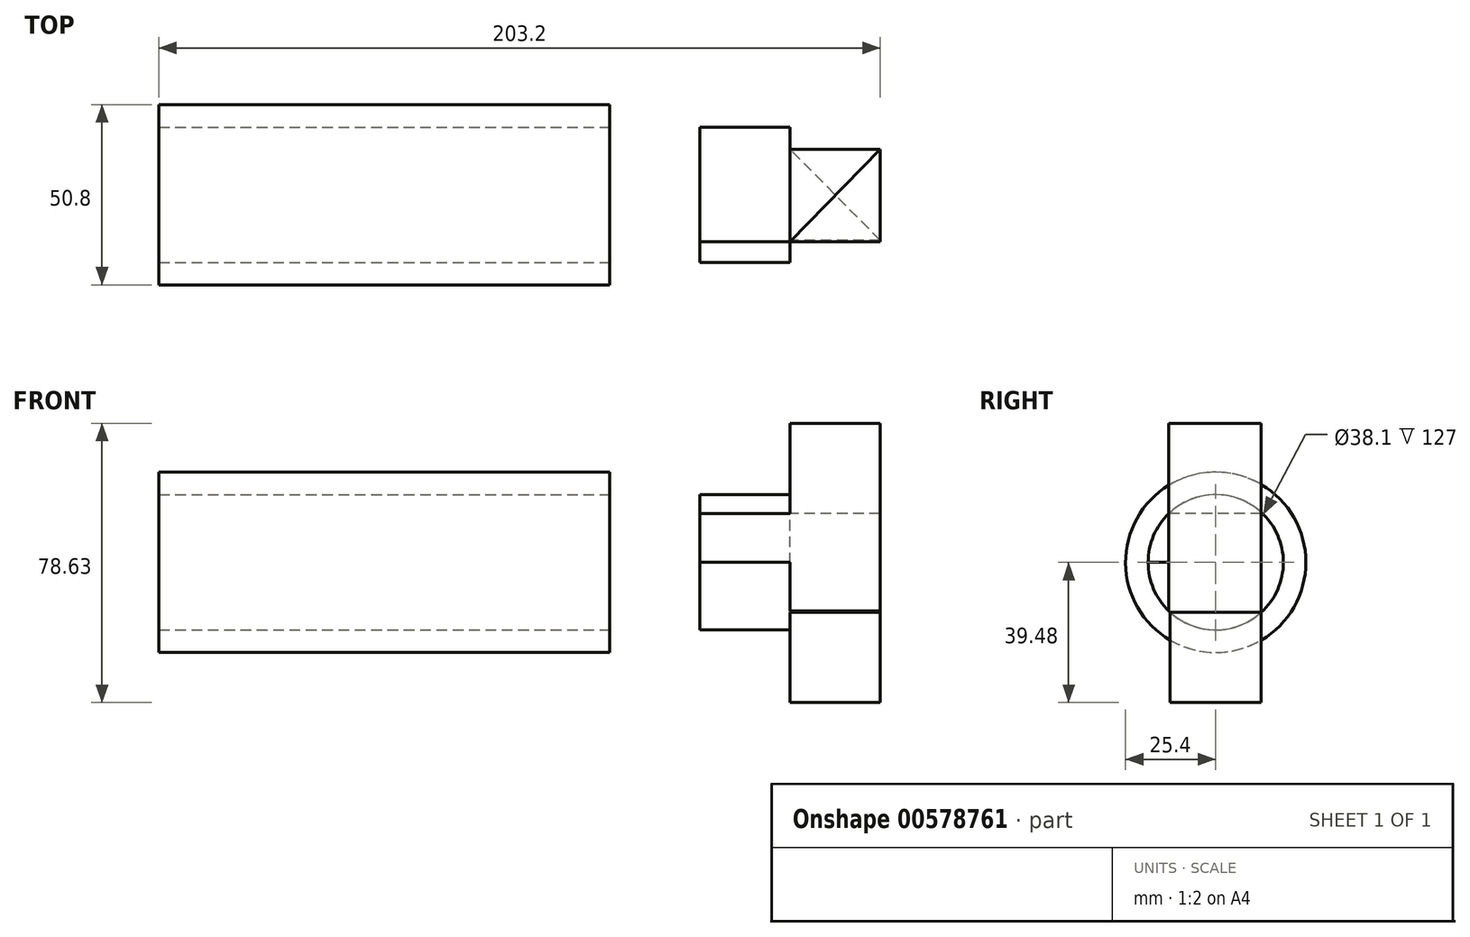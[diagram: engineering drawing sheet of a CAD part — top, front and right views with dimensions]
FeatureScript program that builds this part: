
annotation { "Feature Type Name" : "Feature", "Feature Type Description" : "" }
export const myFeature = defineFeature(function(context is Context, id is Id, definition is map)
    precondition{}
    {
        {
            var Q0;
            Q0=qCreatedBy(makeId("Right.planeOp"),FACE);
            var sketch = newSketch(context, id + "F0", { "sketchPlane" : qUnion([Q0])});
            skCircle(sketch, "E0", {"center": v(0, 0) * mm, "radius": 19.05 * mm});
            skLineSegment(sketch, "E1", {"start": v(19.05, 0) * mm, "end": v(0, 0) * mm});
            skLineSegment(sketch, "E2", {"start": v(0, 0) * mm, "end": v(-19.05, 0) * mm});
            skLineSegment(sketch, "E3", {"start": v(-19.05, 0) * mm, "end": v(0, 0) * mm});
            skLineSegment(sketch, "E4", {"start": v(0, 19.05) * mm, "end": v(0, 0) * mm});
            skLineSegment(sketch, "E5", {"start": v(0, 0) * mm, "end": v(0, -19.05) * mm});
            skLineSegment(sketch, "E6.bottom", {"start": v(12.83, -14.08) * mm, "end": v(-13.18, -14.08) * mm});
            skLineSegment(sketch, "E6.top", {"start": v(12.83, 13.75) * mm, "end": v(-13.18, 13.75) * mm});
            skLineSegment(sketch, "E6.left", {"start": v(12.83, -14.08) * mm, "end": v(12.83, 13.75) * mm});
            skLineSegment(sketch, "E6.right", {"start": v(-13.18, -14.08) * mm, "end": v(-13.18, 13.75) * mm});
            skSolve(sketch);
        }
        {
            var Q0;
            {var subQ0=sQuery(id+"F0.wireOp",EDGE,"E5");var subQ5=sQuery(id+"F0.wireOp",EDGE,"E6.bottom");var subQ6=makeQuery(id+"F0.imprint","INTERSECT",VERTEX,{"derivedFrom":[subQ0,subQ5]});Q0=makeQuery(id+"F0.imprint","IMPRINT",FACE,{"disambiguationData":[TD([[makeQuery(id+"F0.imprint","IMPRINT",EDGE,{"disambiguationData":[TD([[subQ6,1.0]])],"derivedFrom":subQ5}),-1.0]])]});}
            var Q1;
            {var subQ1=sQuery(id+"F0.wireOp",EDGE,"E0");var subQ7=sQuery(id+"F0.wireOp",EDGE,"E6.right");var subQ9=makeQuery(id+"F0.imprint","INTERSECT",VERTEX,{"derivedFrom":[subQ1,subQ7]});Q1=makeQuery(id+"F0.imprint","IMPRINT",FACE,{"disambiguationData":[TD([[makeQuery(id+"F0.imprint","IMPRINT",EDGE,{"disambiguationData":[TD([[subQ9,-1.0]])],"derivedFrom":subQ1}),1.0]])]});}
            var Q2;
            {var subQ0=sQuery(id+"F0.wireOp",EDGE,"E4");var subQ5=sQuery(id+"F0.wireOp",EDGE,"E6.top");var subQ6=makeQuery(id+"F0.imprint","INTERSECT",VERTEX,{"derivedFrom":[subQ0,subQ5]});Q2=makeQuery(id+"F0.imprint","IMPRINT",FACE,{"disambiguationData":[TD([[makeQuery(id+"F0.imprint","IMPRINT",EDGE,{"disambiguationData":[TD([[subQ6,-1.0]])],"derivedFrom":subQ5}),1.0]])]});}
            var Q3;
            {var subQ3=sQuery(id+"F0.wireOp",EDGE,"E6.left");var subQ5=sQuery(id+"F0.wireOp",EDGE,"E6.top");var subQ6=makeQuery(id+"F0.imprint","INTERSECT",VERTEX,{"derivedFrom":[subQ5,subQ3]});Q3=makeQuery(id+"F0.imprint","IMPRINT",FACE,{"disambiguationData":[TD([[makeQuery(id+"F0.imprint","IMPRINT",EDGE,{"disambiguationData":[TD([[subQ6,-1.0]])],"derivedFrom":subQ5}),1.0]])]});}
            extrude(context, id + "F1", {"entities" : qUnion([Q0, Q1, Q2, Q3]), "depth" : 25.4 * mm, "offsetDistance" : 25.4 * mm});
        }
        {
            var Q0;
            {var subQ0=sQuery(id+"F0.wireOp",EDGE,"E5");var subQ1=sQuery(id+"F0.wireOp",EDGE,"E0");var subQ2=makeQuery(id+"F0.imprint","INTERSECT",VERTEX,{"derivedFrom":[subQ1,subQ0]});Q0=makeQuery(id+"F0.imprint","IMPRINT",FACE,{"disambiguationData":[TD([[makeQuery(id+"F0.imprint","IMPRINT",EDGE,{"disambiguationData":[TD([[subQ2,1.0]])],"derivedFrom":subQ1}),1.0]])]});}
            var Q1;
            {var subQ0=sQuery(id+"F0.wireOp",EDGE,"E5");var subQ1=sQuery(id+"F0.wireOp",EDGE,"E0");var subQ2=makeQuery(id+"F0.imprint","INTERSECT",VERTEX,{"derivedFrom":[subQ1,subQ0]});Q1=makeQuery(id+"F0.imprint","IMPRINT",FACE,{"disambiguationData":[TD([[makeQuery(id+"F0.imprint","IMPRINT",EDGE,{"disambiguationData":[TD([[subQ2,1.0]])],"derivedFrom":subQ0}),1.0]])]});}
            var Q2;
            {var subQ0=sQuery(id+"F0.wireOp",EDGE,"E1");var subQ1=sQuery(id+"F0.wireOp",EDGE,"E0");var subQ2=makeQuery(id+"F0.imprint","INTERSECT",VERTEX,{"derivedFrom":[subQ1,subQ0]});Q2=makeQuery(id+"F0.imprint","IMPRINT",FACE,{"disambiguationData":[TD([[makeQuery(id+"F0.imprint","IMPRINT",EDGE,{"disambiguationData":[TD([[subQ2,-1.0]])],"derivedFrom":subQ0}),1.0]])]});}
            var Q3;
            {var subQ0=sQuery(id+"F0.wireOp",EDGE,"E5");var subQ5=sQuery(id+"F0.wireOp",EDGE,"E6.bottom");var subQ6=makeQuery(id+"F0.imprint","INTERSECT",VERTEX,{"derivedFrom":[subQ0,subQ5]});Q3=makeQuery(id+"F0.imprint","IMPRINT",FACE,{"disambiguationData":[TD([[makeQuery(id+"F0.imprint","IMPRINT",EDGE,{"disambiguationData":[TD([[subQ6,1.0]])],"derivedFrom":subQ5}),-1.0]])]});}
            var Q4;
            {var subQ1=sQuery(id+"F0.wireOp",EDGE,"E0");var subQ7=sQuery(id+"F0.wireOp",EDGE,"E6.right");var subQ9=makeQuery(id+"F0.imprint","INTERSECT",VERTEX,{"derivedFrom":[subQ1,subQ7]});Q4=makeQuery(id+"F0.imprint","IMPRINT",FACE,{"disambiguationData":[TD([[makeQuery(id+"F0.imprint","IMPRINT",EDGE,{"disambiguationData":[TD([[subQ9,-1.0]])],"derivedFrom":subQ1}),1.0]])]});}
            var Q5;
            {var subQ0=sQuery(id+"F0.wireOp",EDGE,"E3");var subQ1=sQuery(id+"F0.wireOp",EDGE,"E0");var subQ2=makeQuery(id+"F0.imprint","INTERSECT",VERTEX,{"derivedFrom":[subQ1,subQ0]});Q5=makeQuery(id+"F0.imprint","IMPRINT",FACE,{"disambiguationData":[TD([[makeQuery(id+"F0.imprint","IMPRINT",EDGE,{"disambiguationData":[TD([[subQ2,-1.0]])],"derivedFrom":subQ1}),1.0]])]});}
            var Q6;
            {var subQ0=sQuery(id+"F0.wireOp",EDGE,"E3");var subQ1=sQuery(id+"F0.wireOp",EDGE,"E0");var subQ2=makeQuery(id+"F0.imprint","INTERSECT",VERTEX,{"derivedFrom":[subQ1,subQ0]});Q6=makeQuery(id+"F0.imprint","IMPRINT",FACE,{"disambiguationData":[TD([[makeQuery(id+"F0.imprint","IMPRINT",EDGE,{"disambiguationData":[TD([[subQ2,-1.0]])],"derivedFrom":subQ0}),1.0]])]});}
            var Q7;
            {var subQ0=sQuery(id+"F0.wireOp",EDGE,"E4");var subQ5=sQuery(id+"F0.wireOp",EDGE,"E6.top");var subQ6=makeQuery(id+"F0.imprint","INTERSECT",VERTEX,{"derivedFrom":[subQ0,subQ5]});Q7=makeQuery(id+"F0.imprint","IMPRINT",FACE,{"disambiguationData":[TD([[makeQuery(id+"F0.imprint","IMPRINT",EDGE,{"disambiguationData":[TD([[subQ6,-1.0]])],"derivedFrom":subQ5}),1.0]])]});}
            var Q8;
            {var subQ0=sQuery(id+"F0.wireOp",EDGE,"E4");var subQ1=sQuery(id+"F0.wireOp",EDGE,"E0");var subQ2=makeQuery(id+"F0.imprint","INTERSECT",VERTEX,{"derivedFrom":[subQ1,subQ0]});Q8=makeQuery(id+"F0.imprint","IMPRINT",FACE,{"disambiguationData":[TD([[makeQuery(id+"F0.imprint","IMPRINT",EDGE,{"disambiguationData":[TD([[subQ2,-1.0]])],"derivedFrom":subQ0}),-1.0]])]});}
            var Q9;
            {var subQ5=sQuery(id+"F0.wireOp",EDGE,"E1");var subQ6=sQuery(id+"F0.wireOp",EDGE,"E0");var subQ7=makeQuery(id+"F0.imprint","INTERSECT",VERTEX,{"derivedFrom":[subQ6,subQ5]});Q9=makeQuery(id+"F0.imprint","IMPRINT",FACE,{"disambiguationData":[TD([[makeQuery(id+"F0.imprint","IMPRINT",EDGE,{"disambiguationData":[TD([[subQ7,-1.0]])],"derivedFrom":subQ6}),1.0]])]});}
            var Q10;
            {var subQ3=sQuery(id+"F0.wireOp",EDGE,"E6.left");var subQ5=sQuery(id+"F0.wireOp",EDGE,"E6.top");var subQ6=makeQuery(id+"F0.imprint","INTERSECT",VERTEX,{"derivedFrom":[subQ5,subQ3]});Q10=makeQuery(id+"F0.imprint","IMPRINT",FACE,{"disambiguationData":[TD([[makeQuery(id+"F0.imprint","IMPRINT",EDGE,{"disambiguationData":[TD([[subQ6,-1.0]])],"derivedFrom":subQ5}),1.0]])]});}
            extrude(context, id + "F2", {"entities" : qUnion([Q0, Q1, Q2, Q3, Q4, Q5, Q6, Q7, Q8, Q9, Q10]), "operationType" : NewBodyOperationType.ADD, "oppositeDirection" : true, "depth" : 25.4 * mm, "offsetDistance" : 25.4 * mm});
        }
        {
            var Q0;
            Q0=makeQuery(id+"F1.opExtrude","SWEPT_FACE",FACE,{"disambiguationData":[OSD([sQuery(id+"F0.wireOp",EDGE,"E6.top")])]});
            var sketch = newSketch(context, id + "F3", { "sketchPlane" : qUnion([Q0])});
            skLineSegment(sketch, "E7", {"start": v(0, 12.83) * mm, "end": v(25.4, -13.18) * mm});
            skLineSegment(sketch, "E8", {"start": v(25.4, -13.18) * mm, "end": v(25.4, 12.83) * mm});
            skLineSegment(sketch, "E9", {"start": v(25.4, 12.83) * mm, "end": v(0, -13.18) * mm});
            skCircle(sketch, "E10", {"center": v(12.7, -0.18) * mm, "radius": 3.81 * mm});
            skSolve(sketch);
        }
        {
            var Q0;
            Q0=makeQuery(id+"F1.opExtrude","SWEPT_FACE",FACE,{"disambiguationData":[OSD([sQuery(id+"F0.wireOp",EDGE,"E6.bottom")])]});
            var sketch = newSketch(context, id + "F4", { "sketchPlane" : qUnion([Q0])});
            skLineSegment(sketch, "E11", {"start": v(25.4, -12.83) * mm, "end": v(0, 12.83) * mm});
            skLineSegment(sketch, "E12", {"start": v(0, 12.83) * mm, "end": v(25.4, 12.83) * mm});
            skLineSegment(sketch, "E13", {"start": v(25.4, 12.83) * mm, "end": v(0, -12.83) * mm});
            skCircle(sketch, "E14", {"center": v(12.7, 0) * mm, "radius": 3.81 * mm});
            skSolve(sketch);
        }
        {
            var Q0;
            {var subQ0=sQuery(id+"F3.wireOp",EDGE,"E10");var subQ1=sQuery(id+"F3.wireOp",EDGE,"E7");var subQ2=makeQuery(id+"F3.imprint","INTERSECT",VERTEX,{"disambiguationData":[OD(0.0)],"derivedFrom":[subQ1,subQ0]});Q0=makeQuery(id+"F3.imprint","IMPRINT",FACE,{"disambiguationData":[TD([[makeQuery(id+"F3.imprint","IMPRINT",EDGE,{"disambiguationData":[TD([[subQ2,-1.0]])],"derivedFrom":subQ1}),1.0]])]});}
            var Q1;
            {var subQ0=sQuery(id+"F3.wireOp",EDGE,"E10");var subQ1=sQuery(id+"F3.wireOp",EDGE,"E7");var subQ2=makeQuery(id+"F3.imprint","INTERSECT",VERTEX,{"disambiguationData":[OD(0.0)],"derivedFrom":[subQ1,subQ0]});Q1=makeQuery(id+"F3.imprint","IMPRINT",FACE,{"disambiguationData":[TD([[makeQuery(id+"F3.imprint","IMPRINT",EDGE,{"disambiguationData":[TD([[subQ2,-1.0]])],"derivedFrom":subQ1}),-1.0]])]});}
            var Q2;
            {var subQ0=sQuery(id+"F3.wireOp",EDGE,"E9");var subQ1=sQuery(id+"F3.wireOp",EDGE,"E7");var subQ2=makeQuery(id+"F3.imprint","INTERSECT",VERTEX,{"derivedFrom":[subQ1,subQ0]});Q2=makeQuery(id+"F3.imprint","IMPRINT",FACE,{"disambiguationData":[TD([[makeQuery(id+"F3.imprint","IMPRINT",EDGE,{"disambiguationData":[TD([[subQ2,-1.0]])],"derivedFrom":subQ1}),-1.0]])]});}
            var Q3;
            {var subQ0=sQuery(id+"F3.wireOp",EDGE,"E9");var subQ1=sQuery(id+"F3.wireOp",EDGE,"E7");var subQ2=makeQuery(id+"F3.imprint","INTERSECT",VERTEX,{"derivedFrom":[subQ1,subQ0]});Q3=makeQuery(id+"F3.imprint","IMPRINT",FACE,{"disambiguationData":[TD([[makeQuery(id+"F3.imprint","IMPRINT",EDGE,{"disambiguationData":[TD([[subQ2,-1.0]])],"derivedFrom":subQ1}),1.0]])]});}
            extrude(context, id + "F5", {"entities" : qUnion([Q0, Q1, Q2, Q3]), "operationType" : NewBodyOperationType.ADD, "depth" : 25.4 * mm, "offsetDistance" : 25.4 * mm});
        }
        {
            var Q0;
            {var subQ0=sQuery(id+"F4.wireOp",EDGE,"E14");var subQ1=sQuery(id+"F4.wireOp",EDGE,"E11");var subQ2=makeQuery(id+"F4.imprint","INTERSECT",VERTEX,{"disambiguationData":[OD(0.0)],"derivedFrom":[subQ1,subQ0]});Q0=makeQuery(id+"F4.imprint","IMPRINT",FACE,{"disambiguationData":[TD([[makeQuery(id+"F4.imprint","IMPRINT",EDGE,{"disambiguationData":[TD([[subQ2,-1.0]])],"derivedFrom":subQ1}),1.0]])]});}
            var Q1;
            {var subQ0=sQuery(id+"F4.wireOp",EDGE,"E14");var subQ1=sQuery(id+"F4.wireOp",EDGE,"E11");var subQ2=makeQuery(id+"F4.imprint","INTERSECT",VERTEX,{"disambiguationData":[OD(0.0)],"derivedFrom":[subQ1,subQ0]});Q1=makeQuery(id+"F4.imprint","IMPRINT",FACE,{"disambiguationData":[TD([[makeQuery(id+"F4.imprint","IMPRINT",EDGE,{"disambiguationData":[TD([[subQ2,-1.0]])],"derivedFrom":subQ1}),-1.0]])]});}
            var Q2;
            {var subQ0=sQuery(id+"F4.wireOp",EDGE,"E13");var subQ1=sQuery(id+"F4.wireOp",EDGE,"E11");var subQ2=makeQuery(id+"F4.imprint","INTERSECT",VERTEX,{"derivedFrom":[subQ1,subQ0]});Q2=makeQuery(id+"F4.imprint","IMPRINT",FACE,{"disambiguationData":[TD([[makeQuery(id+"F4.imprint","IMPRINT",EDGE,{"disambiguationData":[TD([[subQ2,-1.0]])],"derivedFrom":subQ1}),-1.0]])]});}
            var Q3;
            {var subQ0=sQuery(id+"F4.wireOp",EDGE,"E13");var subQ1=sQuery(id+"F4.wireOp",EDGE,"E11");var subQ2=makeQuery(id+"F4.imprint","INTERSECT",VERTEX,{"derivedFrom":[subQ1,subQ0]});Q3=makeQuery(id+"F4.imprint","IMPRINT",FACE,{"disambiguationData":[TD([[makeQuery(id+"F4.imprint","IMPRINT",EDGE,{"disambiguationData":[TD([[subQ2,-1.0]])],"derivedFrom":subQ1}),1.0]])]});}
            extrude(context, id + "F6", {"entities" : qUnion([Q0, Q1, Q2, Q3]), "operationType" : NewBodyOperationType.ADD, "depth" : 25.4 * mm, "offsetDistance" : 25.4 * mm});
        }
        {
            var Q0;
            Q0=makeQuery(id+"F2.opExtrude","CAP_FACE",FACE,{"disambiguationData":[OSD([sQuery(id+"F0.wireOp",EDGE,"E0")])],"isStart":false});
            cPlane(context, id + "F7", {"entities" : qUnion([Q0]), "cplaneType" : CPlaneType.OFFSET, "offset" : 25.4 * mm, "width" : 152.4 * mm, "height" : 152.4 * mm});
        }
        {
            var Q0;
            Q0=qCreatedBy(id+"F7.planeOp",FACE);
            var sketch = newSketch(context, id + "F8", { "sketchPlane" : qUnion([Q0])});
            skCircle(sketch, "E15", {"center": v(0, 0) * mm, "radius": 25.4 * mm});
            skSolve(sketch);
        }
        {
            var Q0;
            Q0=makeQuery(id+"F8.imprint","IMPRINT",FACE,{"disambiguationData":[TD([[makeQuery(id+"F8.imprint","IMPRINT",EDGE,{"derivedFrom":sQuery(id+"F8.wireOp",EDGE,"E15")}),1.0]])]});
            extrude(context, id + "F9", {"entities" : qUnion([Q0]), "depth" : 127 * mm, "offsetDistance" : 25.4 * mm});
        }
        {
            var Q0;
            Q0=makeQuery(id+"F9.opExtrude","CAP_FACE",FACE,{"disambiguationData":[OSD([sQuery(id+"F8.wireOp",EDGE,"E15")])],"isStart":true});
            var sketch = newSketch(context, id + "F10", { "sketchPlane" : qUnion([Q0])});
            skLineSegment(sketch, "E16", {"start": v(25.4, 0) * mm, "end": v(-25.4, 0) * mm});
            skLineSegment(sketch, "E17", {"start": v(0, 25.4) * mm, "end": v(0, -25.4) * mm});
            skPoint(sketch, "E18", {"position": v(0, 0) * mm});
            skSolve(sketch);
        }
        {
            var Q0;
            Q0=sQuery(id+"F10.wireOp",VERTEX,"E18");
            var Q1;
            Q1=makeQuery(id+"F9.opExtrude","SWEPT_BODY",BODY,{"disambiguationData":[OSD([sQuery(id+"F8.wireOp",EDGE,"E15")])]});
            hole(context, id + "F11", {"style" : HoleStyle.SIMPLE, "endStyle" : HoleEndStyle.THROUGH, "holeDiameter" : 38.1 * mm, "isTappedThrough" : true, "tappedDepth" : 12.7 * mm, "tapClearance" : 3, "locations" : qUnion([Q0]), "scope" : qUnion([Q1])});
        }
    });
